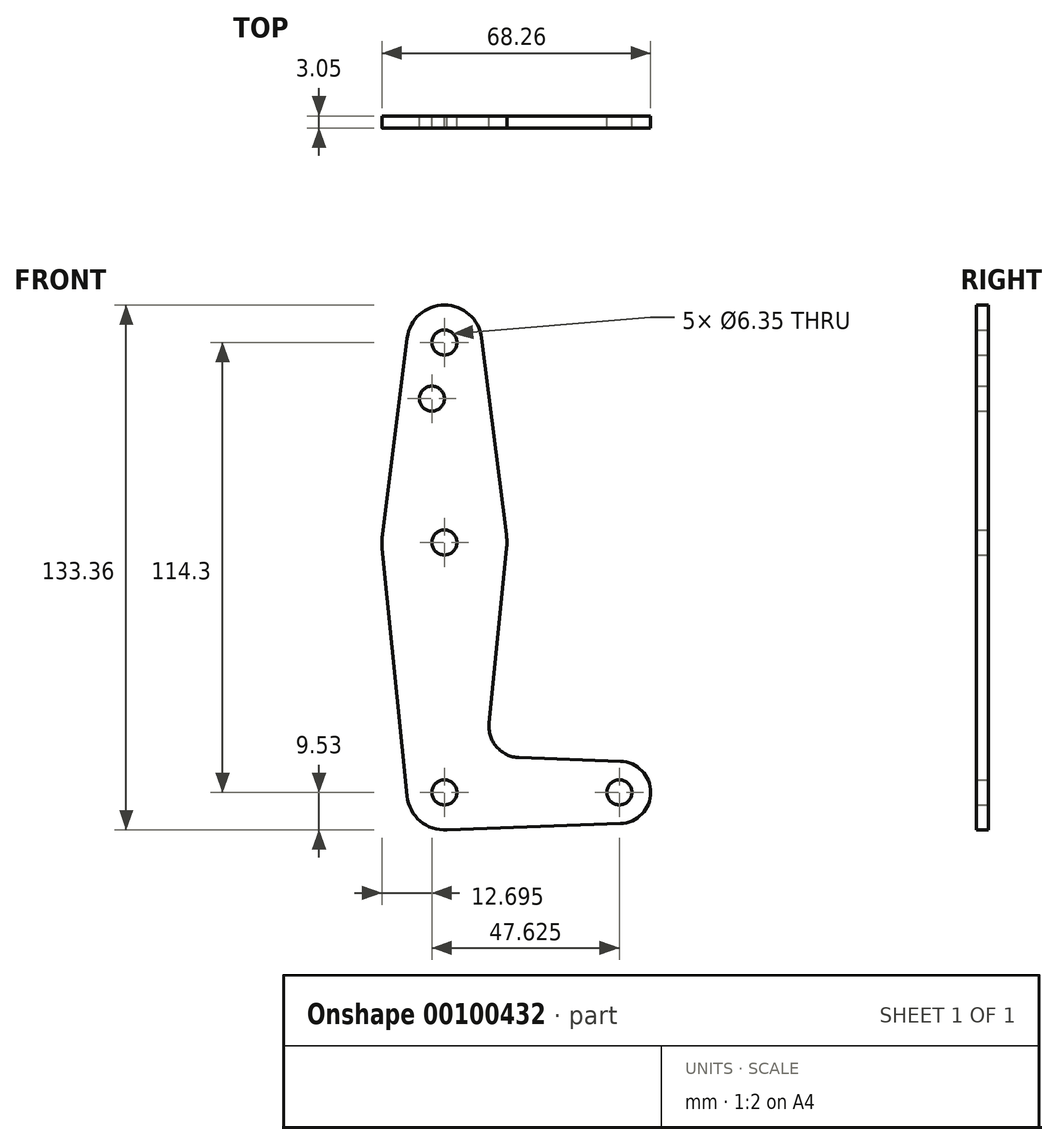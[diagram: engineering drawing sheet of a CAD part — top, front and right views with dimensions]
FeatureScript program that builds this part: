
annotation { "Feature Type Name" : "Feature", "Feature Type Description" : "" }
export const myFeature = defineFeature(function(context is Context, id is Id, definition is map)
    precondition{}
    {
        {
            var Q0;
            Q0=qCreatedBy(makeId("Front.planeOp"),FACE);
            var sketch = newSketch(context, id + "F0", { "sketchPlane" : qUnion([Q0])});
            skLineSegment(sketch, "E0", {"start": v(0, 0) * mm, "end": v(0, 114.3) * mm, "construction": true});
            skLineSegment(sketch, "E1", {"start": v(0, 0) * mm, "end": v(44.45, 0) * mm, "construction": true});
            skCircle(sketch, "E2", {"center": v(0, 114.3) * mm, "radius": 9.53 * mm});
            skCircle(sketch, "E3", {"center": v(44.45, 0) * mm, "radius": 7.94 * mm});
            skCircle(sketch, "E4", {"center": v(0, 0) * mm, "radius": 9.53 * mm});
            skCircle(sketch, "E5", {"center": v(0, 63.5) * mm, "radius": 15.88 * mm});
            skLineSegment(sketch, "E6", {"start": v(-9.45, 115.5) * mm, "end": v(-15.75, 65.48) * mm});
            skLineSegment(sketch, "E7", {"start": v(9.45, 115.5) * mm, "end": v(15.75, 65.48) * mm});
            skLineSegment(sketch, "E8", {"start": v(18.97, 8.85) * mm, "end": v(44.73, 7.93) * mm});
            skLineSegment(sketch, "E9", {"start": v(0, -9.53) * mm, "end": v(44.73, -7.93) * mm});
            skLineSegment(sketch, "E10", {"start": v(-15.8, 61.91) * mm, "end": v(-9.48, -0.95) * mm});
            skLineSegment(sketch, "E11", {"start": v(15.8, 61.91) * mm, "end": v(11.34, 17.59) * mm});
            skCircle(sketch, "E12", {"center": v(0, 114.3) * mm, "radius": 3.18 * mm});
            skCircle(sketch, "E13", {"center": v(0, 63.5) * mm, "radius": 3.18 * mm});
            skCircle(sketch, "E14", {"center": v(0, 0) * mm, "radius": 3.18 * mm});
            skCircle(sketch, "E15", {"center": v(44.45, 0) * mm, "radius": 3.18 * mm});
            skCircle(sketch, "E16", {"center": v(-3.17, 100.03) * mm, "radius": 3.18 * mm});
            skArc(sketch, "E17.filletArc", {"start": v(11.34, 17.59) * mm, "mid": v(13.26, 11.57) * mm, "end": v(18.97, 8.85) * mm});
            skSolve(sketch);
        }
        {
            var Q0;
            Q0 = qSketchRegion(id + "F0", true);
            extrude(context, id + "F1", {"entities" : qUnion([Q0]), "depth" : 3.05 * mm});
        }
    });
